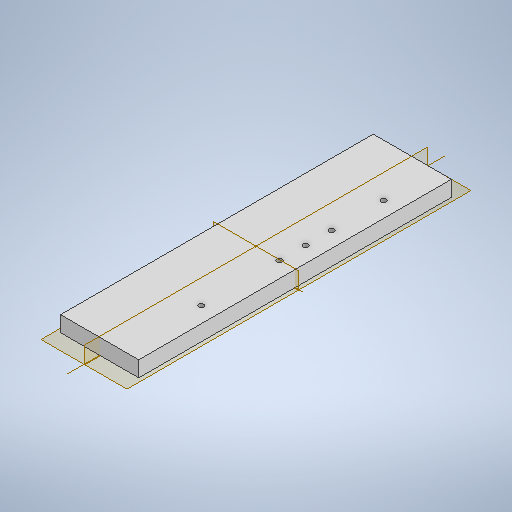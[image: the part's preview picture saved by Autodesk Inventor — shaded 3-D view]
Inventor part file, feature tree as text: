
AUTODESK INVENTOR PART (.ipt)
format: ipt  version: 2025 (Build 290162000, 162)  size: 251,392 bytes
history: native  units: mm
features: pattern_linear x3, sketch x2, extrude x1, hole x1
ambient origin geometry x8: Origin, YZ Plane, XZ Plane, XY Plane, X Axis, Y Axis, Z Axis, Center Point
bodies: Solid1 (feature_tree)
feature tree (7):
  extrude  "Extrusion1"  Depth=300.0mm
  hole  "Hole1"  [1 undecoded]
  pattern_linear  "Rectangular Pattern1"  Count1=5  [1 undecoded]
  pattern_linear  "Rectangular Pattern2"  Count1=2  [1 undecoded]
  pattern_linear  "Rectangular Pattern3"  Count1=2 Spacing1=75.0mm
  sketch  "Sketch1"  dims[d0=75.0mm d1=300.0mm]
  sketch  "Sketch2"  dims[d2=15.0mm d3=0.0mm d4=5.0mm d5=6.0mm d6=4.0mm d7=2.0mm d8=90.0deg d9=10.0mm d10=0.0mm d11=15.0mm d12=50.0mm d13=20.0mm d15=50.0mm d16=20.0mm d18=75.0mm d19=20.0mm d21=100.0mm]
note: 3 required parameter values undecoded (feature->parameter linkage not recoverable at this tier; creation-order binding heuristic only, values carry confidence <= 0.55)
